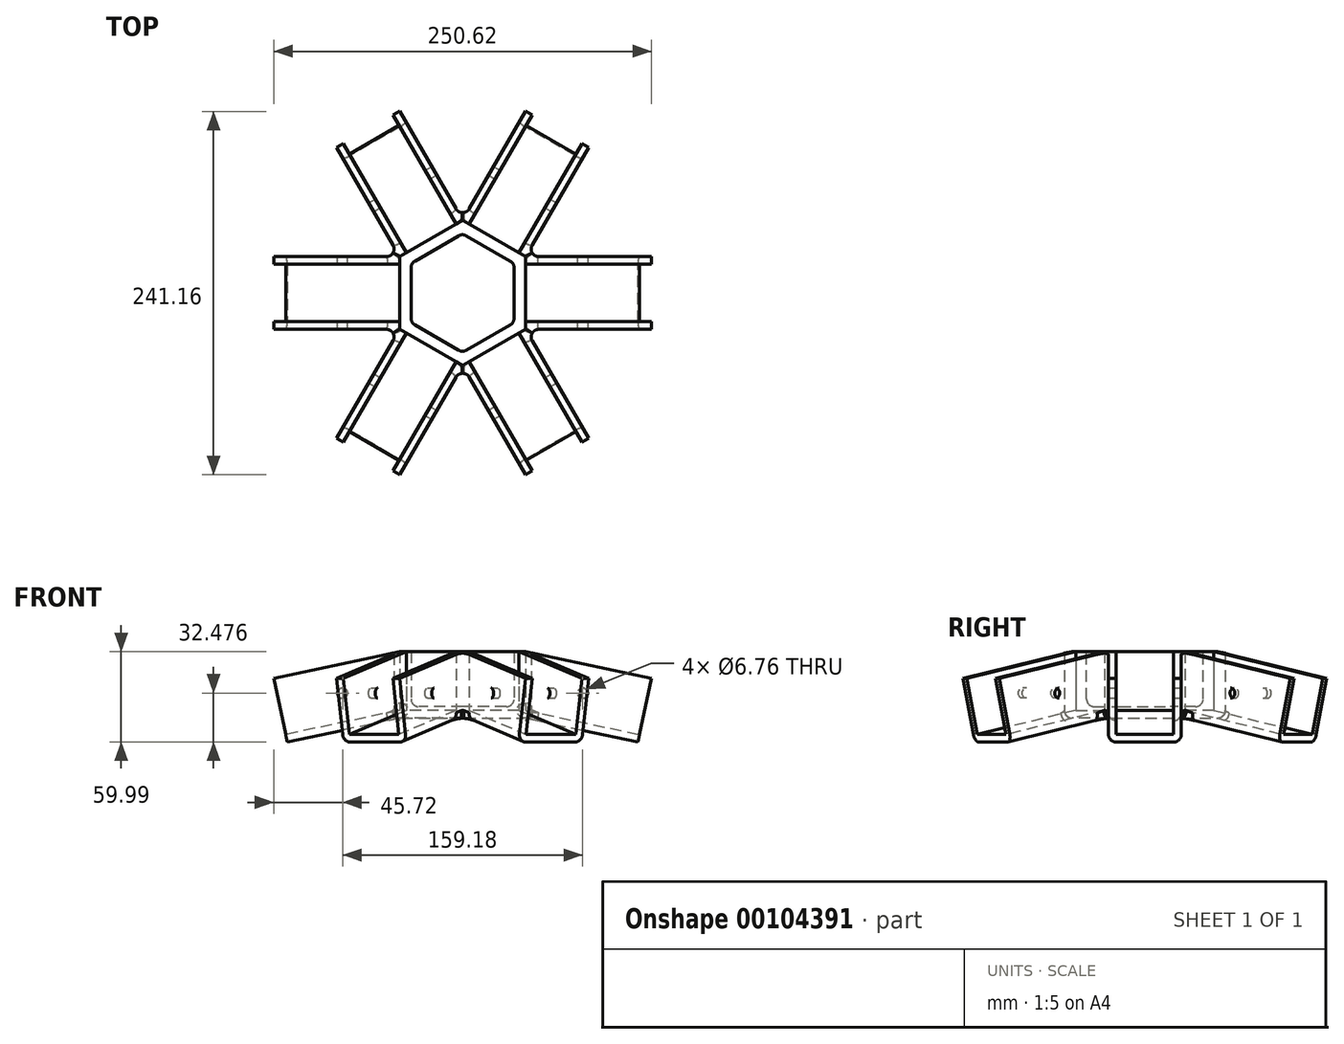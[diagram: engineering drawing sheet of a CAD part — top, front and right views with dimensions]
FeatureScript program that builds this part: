
annotation { "Feature Type Name" : "Feature", "Feature Type Description" : "" }
export const myFeature = defineFeature(function(context is Context, id is Id, definition is map)
    precondition{}
    {
        {
            var Q0;
            Q0=qCreatedBy(makeId("Top.planeOp"),FACE);
            var sketch = newSketch(context, id + "F0", { "sketchPlane" : qUnion([Q0])});
            skCircle(sketch, "E0.cCircle", {"center": v(0, 0) * mm, "radius": 41.8 * mm, "construction": true});
            skLineSegment(sketch, "E0.0", {"start": v(41.8, 24.13) * mm, "end": v(41.8, -24.13) * mm});
            skLineSegment(sketch, "E0.1", {"start": v(41.8, -24.13) * mm, "end": v(0, -48.26) * mm});
            skLineSegment(sketch, "E0.2", {"start": v(0, -48.26) * mm, "end": v(-41.8, -24.13) * mm});
            skLineSegment(sketch, "E0.3", {"start": v(-41.8, -24.13) * mm, "end": v(-41.8, 24.13) * mm});
            skLineSegment(sketch, "E0.4", {"start": v(-41.8, 24.13) * mm, "end": v(0, 48.26) * mm});
            skLineSegment(sketch, "E0.5", {"start": v(0, 48.26) * mm, "end": v(41.8, 24.13) * mm});
            skPoint(sketch, "E0.0.midPoint", {"position": v(41.8, 0) * mm});
            skSolve(sketch);
        }
        {
            var Q0;
            Q0 = qSketchRegion(id + "F0", true);
            extrude(context, id + "F1", {"entities" : qUnion([Q0]), "depth" : 44.15 * mm});
        }
        {
            var Q0;
            Q0=qCreatedBy(makeId("Front.planeOp"),FACE);
            var sketch = newSketch(context, id + "F2", { "sketchPlane" : qUnion([Q0])});
            skLineSegment(sketch, "E1", {"start": v(41.8, 0) * mm, "end": v(116.33, -15.84) * mm});
            skLineSegment(sketch, "E2", {"start": v(116.33, -15.84) * mm, "end": v(125.3, 26.4) * mm});
            skLineSegment(sketch, "E3", {"start": v(125.3, 26.4) * mm, "end": v(41.8, 44.15) * mm});
            skLineSegment(sketch, "E4", {"start": v(41.8, 44.15) * mm, "end": v(41.8, 0) * mm});
            skSolve(sketch);
        }
        {
            var Q0;
            Q0=makeQuery(id+"F2.imprint","IMPRINT",FACE,{"disambiguationData":[TD([[makeQuery(id+"F2.imprint","IMPRINT",EDGE,{"derivedFrom":sQuery(id+"F2.wireOp",EDGE,"E1")}),1.0]])]});
            extrude(context, id + "F3", {"entities" : qUnion([Q0]), "endBound" : BoundingType.SYMMETRIC, "depth" : 48.26 * mm});
        }
        {
            var Q0;
            Q0=makeQuery(id+"F3.opExtrude","SWEPT_FACE",FACE,{"disambiguationData":[OSD([sQuery(id+"F2.wireOp",EDGE,"E3")])]});
            var Q1;
            Q1=makeQuery(id+"F3.opExtrude","SWEPT_FACE",FACE,{"disambiguationData":[OSD([sQuery(id+"F2.wireOp",EDGE,"E2")])]});
            var Q2;
            Q2=makeQuery(id+"F3.opExtrude","SWEPT_FACE",FACE,{"disambiguationData":[OSD([sQuery(id+"F2.wireOp",EDGE,"E4")])]});
            shell(context, id + "F4", {"entities" : qUnion([Q0, Q1, Q2]), "thickness" : 5.08 * mm});
        }
        {
            var Q0;
            Q0=makeQuery(id+"F3.opExtrude","CAP_FACE",FACE,{"disambiguationData":[OSD([sQuery(id+"F2.wireOp",EDGE,"E1"),sQuery(id+"F2.wireOp",EDGE,"E2"),sQuery(id+"F2.wireOp",EDGE,"E3"),sQuery(id+"F2.wireOp",EDGE,"E4")])],"isStart":false});
            var sketch = newSketch(context, id + "F5", { "sketchPlane" : qUnion([Q0])});
            skPoint(sketch, "E5", {"position": v(79.59, 16.64) * mm});
            skLineSegment(sketch, "E6", {"start": v(41.8, 44.15) * mm, "end": v(117.39, -10.87) * mm, "construction": true});
            skSolve(sketch);
        }
        {
            var Q0;
            Q0=sQuery(id+"F5.wireOp",VERTEX,"E5");
            var Q1;
            Q1=makeQuery(id+"F3.opExtrude","SWEPT_BODY",BODY,{"disambiguationData":[OSD([sQuery(id+"F2.wireOp",EDGE,"E1"),sQuery(id+"F2.wireOp",EDGE,"E2"),sQuery(id+"F2.wireOp",EDGE,"E3"),sQuery(id+"F2.wireOp",EDGE,"E4")])]});
            hole(context, id + "F6", {"style" : HoleStyle.SIMPLE, "endStyle" : HoleEndStyle.THROUGH, "standardTappedOrClearance" : lookupTablePath({ "standard" : "ANSI", "fit" : "Normal (ASME)", "size" : "1/4", "type" : "Clearance" }), "standardBlindInLast" : lookupTablePath({ "fit" : "Free", "standard" : "ANSI", "size" : "1/4", "type" : "Clearance" }), "holeDiameter" : 6.76 * mm, "locations" : qUnion([Q0]), "scope" : qUnion([Q1]), "isTappedThrough" : true});
        }
        {
            var Q0;
            Q0=qCreatedBy(makeId("Front.planeOp"),FACE);
            var sketch = newSketch(context, id + "F7", { "sketchPlane" : qUnion([Q0])});
            skLineSegment(sketch, "E7", {"start": v(0, 0) * mm, "end": v(0, 66.69) * mm, "construction": true});
            skSolve(sketch);
        }
        {
            var Q0;
            Q0=makeQuery(id+"F3.opExtrude","SWEPT_BODY",BODY,{"disambiguationData":[OSD([sQuery(id+"F2.wireOp",EDGE,"E1"),sQuery(id+"F2.wireOp",EDGE,"E2"),sQuery(id+"F2.wireOp",EDGE,"E3"),sQuery(id+"F2.wireOp",EDGE,"E4")])]});
            var Q1;
            Q1=sQuery(id+"F7.wireOp",EDGE,"E7");
            circularPattern(context, id + "F8", {"entities" : qUnion([Q0]), "axis" : qUnion([Q1]), "angle" : 60 * degree, "instanceCount" : 6});
        }
        {
            var Q0;
            Q0=makeQuery(id+"F1.opExtrude","CAP_FACE",FACE,{"disambiguationData":[OSD([sQuery(id+"F0.wireOp",EDGE,"E0.0"),sQuery(id+"F0.wireOp",EDGE,"E0.1"),sQuery(id+"F0.wireOp",EDGE,"E0.2"),sQuery(id+"F0.wireOp",EDGE,"E0.3"),sQuery(id+"F0.wireOp",EDGE,"E0.4"),sQuery(id+"F0.wireOp",EDGE,"E0.5")])],"isStart":false});
            shell(context, id + "F9", {"entities" : qUnion([Q0]), "thickness" : 7.62 * mm});
        }
        {
            var Q0;
            Q0=makeQuery(id+"F8.opPattern","COPY",BODY,{"derivedFrom":makeQuery(id+"F3.opExtrude","SWEPT_BODY",BODY,{"disambiguationData":[OSD([sQuery(id+"F2.wireOp",EDGE,"E1"),sQuery(id+"F2.wireOp",EDGE,"E2"),sQuery(id+"F2.wireOp",EDGE,"E3"),sQuery(id+"F2.wireOp",EDGE,"E4")])]}),"instanceName":"3"});
            var Q1;
            Q1=makeQuery(id+"F8.opPattern","COPY",BODY,{"derivedFrom":makeQuery(id+"F3.opExtrude","SWEPT_BODY",BODY,{"disambiguationData":[OSD([sQuery(id+"F2.wireOp",EDGE,"E1"),sQuery(id+"F2.wireOp",EDGE,"E2"),sQuery(id+"F2.wireOp",EDGE,"E3"),sQuery(id+"F2.wireOp",EDGE,"E4")])]}),"instanceName":"2"});
            var Q2;
            Q2=makeQuery(id+"F8.opPattern","COPY",BODY,{"derivedFrom":makeQuery(id+"F3.opExtrude","SWEPT_BODY",BODY,{"disambiguationData":[OSD([sQuery(id+"F2.wireOp",EDGE,"E1"),sQuery(id+"F2.wireOp",EDGE,"E2"),sQuery(id+"F2.wireOp",EDGE,"E3"),sQuery(id+"F2.wireOp",EDGE,"E4")])]}),"instanceName":"1"});
            var Q3;
            Q3=makeQuery(id+"F3.opExtrude","SWEPT_BODY",BODY,{"disambiguationData":[OSD([sQuery(id+"F2.wireOp",EDGE,"E1"),sQuery(id+"F2.wireOp",EDGE,"E2"),sQuery(id+"F2.wireOp",EDGE,"E3"),sQuery(id+"F2.wireOp",EDGE,"E4")])]});
            var Q4;
            Q4=makeQuery(id+"F8.opPattern","COPY",BODY,{"derivedFrom":makeQuery(id+"F3.opExtrude","SWEPT_BODY",BODY,{"disambiguationData":[OSD([sQuery(id+"F2.wireOp",EDGE,"E1"),sQuery(id+"F2.wireOp",EDGE,"E2"),sQuery(id+"F2.wireOp",EDGE,"E3"),sQuery(id+"F2.wireOp",EDGE,"E4")])]}),"instanceName":"5"});
            var Q5;
            Q5=makeQuery(id+"F8.opPattern","COPY",BODY,{"derivedFrom":makeQuery(id+"F3.opExtrude","SWEPT_BODY",BODY,{"disambiguationData":[OSD([sQuery(id+"F2.wireOp",EDGE,"E1"),sQuery(id+"F2.wireOp",EDGE,"E2"),sQuery(id+"F2.wireOp",EDGE,"E3"),sQuery(id+"F2.wireOp",EDGE,"E4")])]}),"instanceName":"4"});
            var Q6;
            Q6=makeQuery(id+"F1.opExtrude","SWEPT_BODY",BODY,{"disambiguationData":[OSD([sQuery(id+"F0.wireOp",EDGE,"E0.0"),sQuery(id+"F0.wireOp",EDGE,"E0.1"),sQuery(id+"F0.wireOp",EDGE,"E0.2"),sQuery(id+"F0.wireOp",EDGE,"E0.3"),sQuery(id+"F0.wireOp",EDGE,"E0.4"),sQuery(id+"F0.wireOp",EDGE,"E0.5")])]});
            booleanBodies(context, id + "F10", {"operationType" : BooleanOperationType.UNION, "tools" : qUnion([Q0, Q1, Q2, Q3, Q4, Q5, Q6])});
        }
        {
            var Q0;
            Q0=makeQuery(id+"F9.opShell","OFFSET_EDGE",EDGE,{"disambiguationData":[OSD([sQuery(id+"F0.wireOp",EDGE,"E0.4"),sQuery(id+"F0.wireOp",EDGE,"E0.5")])]});
            var Q1;
            Q1=makeQuery(id+"F9.opShell","OFFSET_EDGE",EDGE,{"disambiguationData":[OSD([sQuery(id+"F0.wireOp",EDGE,"E0.0"),sQuery(id+"F0.wireOp",EDGE,"E0.5")])]});
            var Q2;
            Q2=makeQuery(id+"F9.opShell","OFFSET_EDGE",EDGE,{"disambiguationData":[OSD([sQuery(id+"F0.wireOp",EDGE,"E0.0"),sQuery(id+"F0.wireOp",EDGE,"E0.1")])]});
            var Q3;
            Q3=makeQuery(id+"F9.opShell","OFFSET_EDGE",EDGE,{"disambiguationData":[OSD([sQuery(id+"F0.wireOp",EDGE,"E0.1"),sQuery(id+"F0.wireOp",EDGE,"E0.2")])]});
            var Q4;
            Q4=makeQuery(id+"F9.opShell","OFFSET_EDGE",EDGE,{"disambiguationData":[OSD([sQuery(id+"F0.wireOp",EDGE,"E0.2"),sQuery(id+"F0.wireOp",EDGE,"E0.3")])]});
            var Q5;
            Q5=makeQuery(id+"F9.opShell","OFFSET_EDGE",EDGE,{"disambiguationData":[OSD([sQuery(id+"F0.wireOp",EDGE,"E0.3"),sQuery(id+"F0.wireOp",EDGE,"E0.4")])]});
            fillet(context, id + "F11", {"entities" : qUnion([Q0, Q1, Q2, Q3, Q4, Q5]), "radius" : 5.08 * mm, "tangentPropagation" : true, "allowEdgeOverflow" : false});
        }
        {
            var Q0;
            {var subQ0=sQuery(id+"F2.wireOp",EDGE,"E4");Q0=makeQuery(id+"F10.opBoolean","MERGE",EDGE,{"derivedFrom":[makeQuery(id+"F1.opExtrude","SWEPT_EDGE",EDGE,{"disambiguationData":[OSD([sQuery(id+"F0.wireOp",EDGE,"E0.1"),sQuery(id+"F0.wireOp",EDGE,"E0.2")])]}),makeQuery(id+"F8.opPattern","COPY",EDGE,{"derivedFrom":makeQuery(id+"F3.opExtrude","CAP_EDGE",EDGE,{"disambiguationData":[OSD([subQ0])],"isStart":true}),"instanceName":"4"}),makeQuery(id+"F8.opPattern","COPY",EDGE,{"derivedFrom":makeQuery(id+"F3.opExtrude","CAP_EDGE",EDGE,{"disambiguationData":[OSD([subQ0])],"isStart":false}),"instanceName":"5"})]});}
            var Q1;
            {var subQ0=sQuery(id+"F2.wireOp",EDGE,"E4");Q1=makeQuery(id+"F10.opBoolean","MERGE",EDGE,{"derivedFrom":[makeQuery(id+"F1.opExtrude","SWEPT_EDGE",EDGE,{"disambiguationData":[OSD([sQuery(id+"F0.wireOp",EDGE,"E0.0"),sQuery(id+"F0.wireOp",EDGE,"E0.1")])]}),makeQuery(id+"F3.opExtrude","CAP_EDGE",EDGE,{"disambiguationData":[OSD([subQ0])],"isStart":false}),makeQuery(id+"F8.opPattern","COPY",EDGE,{"derivedFrom":makeQuery(id+"F3.opExtrude","CAP_EDGE",EDGE,{"disambiguationData":[OSD([subQ0])],"isStart":true}),"instanceName":"5"})]});}
            var Q2;
            {var subQ0=sQuery(id+"F2.wireOp",EDGE,"E4");Q2=makeQuery(id+"F10.opBoolean","MERGE",EDGE,{"derivedFrom":[makeQuery(id+"F1.opExtrude","SWEPT_EDGE",EDGE,{"disambiguationData":[OSD([sQuery(id+"F0.wireOp",EDGE,"E0.0"),sQuery(id+"F0.wireOp",EDGE,"E0.5")])]}),makeQuery(id+"F3.opExtrude","CAP_EDGE",EDGE,{"disambiguationData":[OSD([subQ0])],"isStart":true}),makeQuery(id+"F8.opPattern","COPY",EDGE,{"derivedFrom":makeQuery(id+"F3.opExtrude","CAP_EDGE",EDGE,{"disambiguationData":[OSD([subQ0])],"isStart":false}),"instanceName":"1"})]});}
            var Q3;
            {var subQ0=sQuery(id+"F2.wireOp",EDGE,"E4");Q3=makeQuery(id+"F10.opBoolean","MERGE",EDGE,{"derivedFrom":[makeQuery(id+"F1.opExtrude","SWEPT_EDGE",EDGE,{"disambiguationData":[OSD([sQuery(id+"F0.wireOp",EDGE,"E0.4"),sQuery(id+"F0.wireOp",EDGE,"E0.5")])]}),makeQuery(id+"F8.opPattern","COPY",EDGE,{"derivedFrom":makeQuery(id+"F3.opExtrude","CAP_EDGE",EDGE,{"disambiguationData":[OSD([subQ0])],"isStart":true}),"instanceName":"1"}),makeQuery(id+"F8.opPattern","COPY",EDGE,{"derivedFrom":makeQuery(id+"F3.opExtrude","CAP_EDGE",EDGE,{"disambiguationData":[OSD([subQ0])],"isStart":false}),"instanceName":"2"})]});}
            var Q4;
            {var subQ0=sQuery(id+"F2.wireOp",EDGE,"E4");Q4=makeQuery(id+"F10.opBoolean","MERGE",EDGE,{"derivedFrom":[makeQuery(id+"F1.opExtrude","SWEPT_EDGE",EDGE,{"disambiguationData":[OSD([sQuery(id+"F0.wireOp",EDGE,"E0.3"),sQuery(id+"F0.wireOp",EDGE,"E0.4")])]}),makeQuery(id+"F8.opPattern","COPY",EDGE,{"derivedFrom":makeQuery(id+"F3.opExtrude","CAP_EDGE",EDGE,{"disambiguationData":[OSD([subQ0])],"isStart":true}),"instanceName":"2"}),makeQuery(id+"F8.opPattern","COPY",EDGE,{"derivedFrom":makeQuery(id+"F3.opExtrude","CAP_EDGE",EDGE,{"disambiguationData":[OSD([subQ0])],"isStart":false}),"instanceName":"3"})]});}
            var Q5;
            {var subQ0=sQuery(id+"F2.wireOp",EDGE,"E4");Q5=makeQuery(id+"F10.opBoolean","MERGE",EDGE,{"derivedFrom":[makeQuery(id+"F1.opExtrude","SWEPT_EDGE",EDGE,{"disambiguationData":[OSD([sQuery(id+"F0.wireOp",EDGE,"E0.2"),sQuery(id+"F0.wireOp",EDGE,"E0.3")])]}),makeQuery(id+"F8.opPattern","COPY",EDGE,{"derivedFrom":makeQuery(id+"F3.opExtrude","CAP_EDGE",EDGE,{"disambiguationData":[OSD([subQ0])],"isStart":true}),"instanceName":"3"}),makeQuery(id+"F8.opPattern","COPY",EDGE,{"derivedFrom":makeQuery(id+"F3.opExtrude","CAP_EDGE",EDGE,{"disambiguationData":[OSD([subQ0])],"isStart":false}),"instanceName":"4"})]});}
            fillet(context, id + "F12", {"entities" : qUnion([Q0, Q1, Q2, Q3, Q4, Q5]), "radius" : 5.08 * mm, "tangentPropagation" : true, "allowEdgeOverflow" : false});
        }
        {
            var Q0;
            {var subQ0=sQuery(id+"F0.wireOp",EDGE,"E0.3");Q0=makeQuery(id+"F9.opShell","OFFSET_EDGE",EDGE,{"disambiguationData":[OSD([subQ0]),TDD([makeQuery(id+"F1.opExtrude","CAP_EDGE",EDGE,{"disambiguationData":[OSD([subQ0])],"isStart":true})])]});}
            fillet(context, id + "F13", {"entities" : qUnion([Q0]), "radius" : 5.08 * mm, "tangentPropagation" : true, "allowEdgeOverflow" : false});
        }
        {
            var Q0;
            Q0=makeQuery(id+"F8.opPattern","COPY",EDGE,{"derivedFrom":makeQuery(id+"F3.opExtrude","CAP_EDGE",EDGE,{"disambiguationData":[OSD([sQuery(id+"F2.wireOp",EDGE,"E1")])],"isStart":false}),"instanceName":"1"});
            var Q1;
            Q1=makeQuery(id+"F3.opExtrude","CAP_EDGE",EDGE,{"disambiguationData":[OSD([sQuery(id+"F2.wireOp",EDGE,"E1")])],"isStart":true});
            var Q2;
            Q2=makeQuery(id+"F8.opPattern","COPY",EDGE,{"derivedFrom":makeQuery(id+"F3.opExtrude","CAP_EDGE",EDGE,{"disambiguationData":[OSD([sQuery(id+"F2.wireOp",EDGE,"E1")])],"isStart":true}),"instanceName":"1"});
            var Q3;
            Q3=makeQuery(id+"F8.opPattern","COPY",EDGE,{"derivedFrom":makeQuery(id+"F3.opExtrude","CAP_EDGE",EDGE,{"disambiguationData":[OSD([sQuery(id+"F2.wireOp",EDGE,"E1")])],"isStart":false}),"instanceName":"2"});
            var Q4;
            Q4=makeQuery(id+"F8.opPattern","COPY",EDGE,{"derivedFrom":makeQuery(id+"F3.opExtrude","CAP_EDGE",EDGE,{"disambiguationData":[OSD([sQuery(id+"F2.wireOp",EDGE,"E1")])],"isStart":true}),"instanceName":"2"});
            var Q5;
            Q5=makeQuery(id+"F8.opPattern","COPY",EDGE,{"derivedFrom":makeQuery(id+"F3.opExtrude","CAP_EDGE",EDGE,{"disambiguationData":[OSD([sQuery(id+"F2.wireOp",EDGE,"E1")])],"isStart":false}),"instanceName":"3"});
            var Q6;
            Q6=makeQuery(id+"F8.opPattern","COPY",EDGE,{"derivedFrom":makeQuery(id+"F3.opExtrude","CAP_EDGE",EDGE,{"disambiguationData":[OSD([sQuery(id+"F2.wireOp",EDGE,"E1")])],"isStart":true}),"instanceName":"3"});
            var Q7;
            Q7=makeQuery(id+"F8.opPattern","COPY",EDGE,{"derivedFrom":makeQuery(id+"F3.opExtrude","CAP_EDGE",EDGE,{"disambiguationData":[OSD([sQuery(id+"F2.wireOp",EDGE,"E1")])],"isStart":false}),"instanceName":"4"});
            var Q8;
            Q8=makeQuery(id+"F8.opPattern","COPY",EDGE,{"derivedFrom":makeQuery(id+"F3.opExtrude","CAP_EDGE",EDGE,{"disambiguationData":[OSD([sQuery(id+"F2.wireOp",EDGE,"E1")])],"isStart":true}),"instanceName":"4"});
            var Q9;
            Q9=makeQuery(id+"F8.opPattern","COPY",EDGE,{"derivedFrom":makeQuery(id+"F3.opExtrude","CAP_EDGE",EDGE,{"disambiguationData":[OSD([sQuery(id+"F2.wireOp",EDGE,"E1")])],"isStart":false}),"instanceName":"5"});
            var Q10;
            Q10=makeQuery(id+"F3.opExtrude","CAP_EDGE",EDGE,{"disambiguationData":[OSD([sQuery(id+"F2.wireOp",EDGE,"E1")])],"isStart":false});
            var Q11;
            Q11=makeQuery(id+"F8.opPattern","COPY",EDGE,{"derivedFrom":makeQuery(id+"F3.opExtrude","CAP_EDGE",EDGE,{"disambiguationData":[OSD([sQuery(id+"F2.wireOp",EDGE,"E1")])],"isStart":true}),"instanceName":"5"});
            fillet(context, id + "F14", {"entities" : qUnion([Q0, Q1, Q2, Q3, Q4, Q5, Q6, Q7, Q8, Q9, Q10, Q11]), "radius" : 5.08 * mm, "tangentPropagation" : true, "allowEdgeOverflow" : false});
        }
    });
